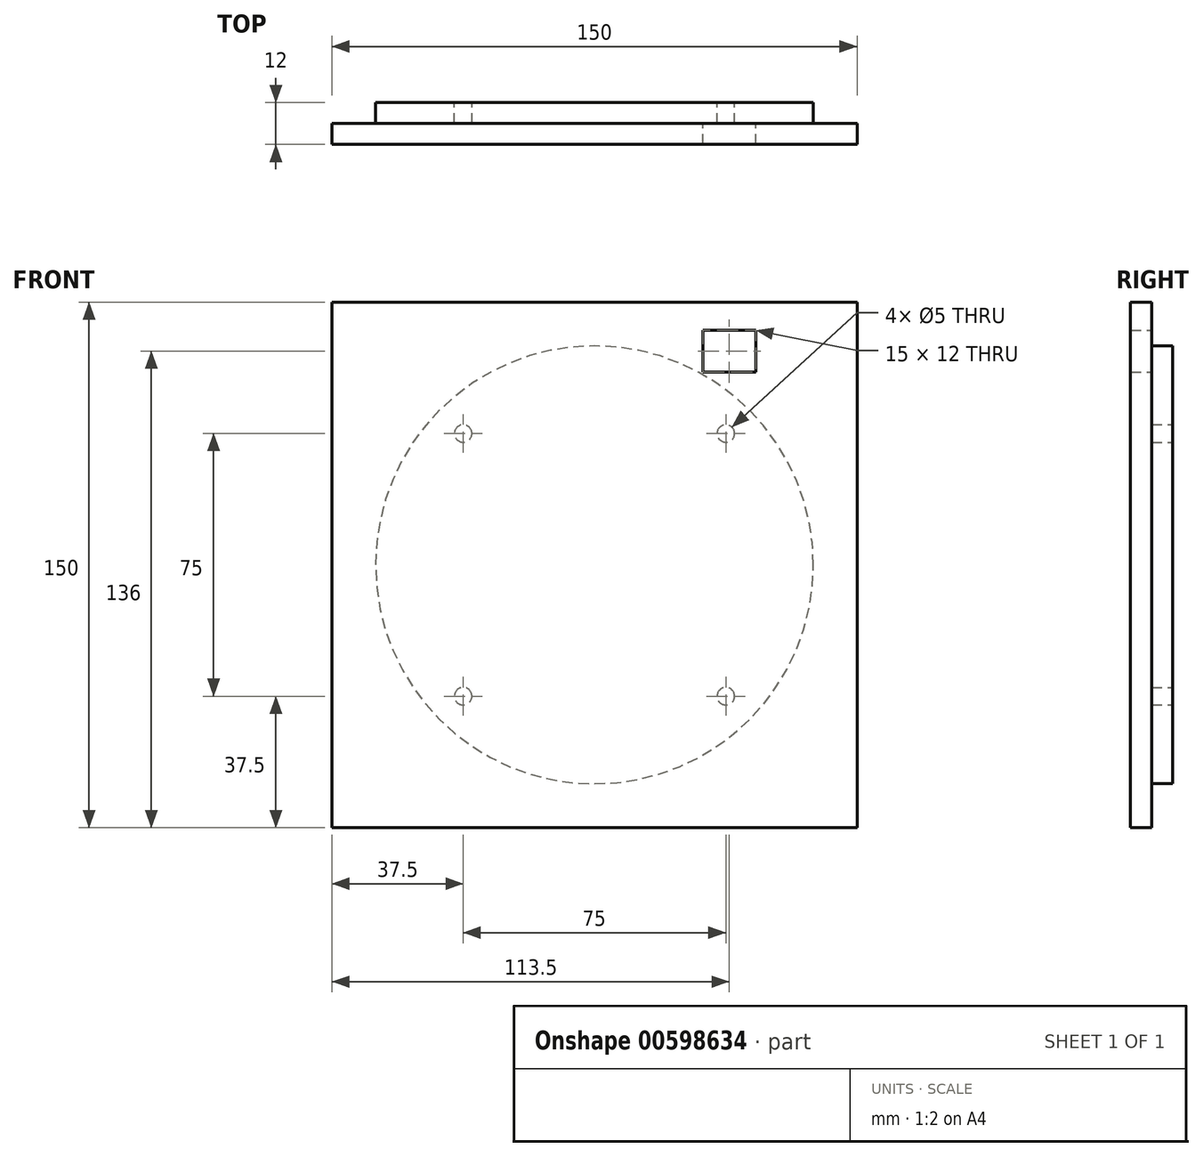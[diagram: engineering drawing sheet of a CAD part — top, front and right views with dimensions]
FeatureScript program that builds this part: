
annotation { "Feature Type Name" : "Feature", "Feature Type Description" : "" }
export const myFeature = defineFeature(function(context is Context, id is Id, definition is map)
    precondition{}
    {
        {
            var Q0;
            Q0=qCreatedBy(makeId("Front.planeOp"),FACE);
            var sketch = newSketch(context, id + "F0", { "sketchPlane" : qUnion([Q0])});
            skLineSegment(sketch, "E0.bottom", {"start": v(60, 60) * mm, "end": v(-60, 60) * mm, "construction": true});
            skLineSegment(sketch, "E0.top", {"start": v(60, -60) * mm, "end": v(-60, -60) * mm, "construction": true});
            skLineSegment(sketch, "E0.left", {"start": v(60, 60) * mm, "end": v(60, -60) * mm, "construction": true});
            skLineSegment(sketch, "E0.right", {"start": v(-60, 60) * mm, "end": v(-60, -60) * mm, "construction": true});
            skPoint(sketch, "E0.middle", {"position": v(0, 0) * mm});
            skCircle(sketch, "E1", {"center": v(0, 0) * mm, "radius": 62.5 * mm});
            skCircle(sketch, "E2", {"center": v(37.5, 37.5) * mm, "radius": 2.5 * mm});
            skCircle(sketch, "E3.0.1.0", {"center": v(37.5, -37.5) * mm, "radius": 2.5 * mm});
            skCircle(sketch, "E3.1.0.0", {"center": v(-37.5, 37.5) * mm, "radius": 2.5 * mm});
            skCircle(sketch, "E3.1.1.0", {"center": v(-37.5, -37.5) * mm, "radius": 2.5 * mm});
            skLineSegment(sketch, "E3.direction1", {"start": v(37.5, 37.5) * mm, "end": v(-37.5, 37.5) * mm, "construction": true});
            skLineSegment(sketch, "E3.direction2", {"start": v(37.5, 37.5) * mm, "end": v(37.5, -37.5) * mm, "construction": true});
            skSolve(sketch);
        }
        {
            var Q0;
            Q0 = qSketchRegion(id + "F0", true);
            extrude(context, id + "F1", {"entities" : qUnion([Q0]), "depth" : 6 * mm, "offsetDistance" : 25 * mm});
        }
        {
            var Q0;
            Q0=makeQuery(id+"F1.opExtrude","CAP_FACE",FACE,{"disambiguationData":[OSD([sQuery(id+"F0.wireOp",EDGE,"E1"),sQuery(id+"F0.wireOp",EDGE,"E2"),sQuery(id+"F0.wireOp",EDGE,"E3.0.1.0"),sQuery(id+"F0.wireOp",EDGE,"E3.1.0.0"),sQuery(id+"F0.wireOp",EDGE,"E3.1.1.0")])],"isStart":false});
            var sketch = newSketch(context, id + "F2", { "sketchPlane" : qUnion([Q0])});
            skLineSegment(sketch, "E4.bottom", {"start": v(75, 75) * mm, "end": v(-75, 75) * mm});
            skLineSegment(sketch, "E4.top", {"start": v(75, -75) * mm, "end": v(-75, -75) * mm});
            skLineSegment(sketch, "E4.left", {"start": v(75, 75) * mm, "end": v(75, -75) * mm});
            skLineSegment(sketch, "E4.right", {"start": v(-75, 75) * mm, "end": v(-75, -75) * mm});
            skPoint(sketch, "E4.middle", {"position": v(0, 0) * mm});
            skLineSegment(sketch, "E5.bottom", {"start": v(60, 60) * mm, "end": v(-60, 60) * mm, "construction": true});
            skLineSegment(sketch, "E5.top", {"start": v(60, -60) * mm, "end": v(-60, -60) * mm, "construction": true});
            skLineSegment(sketch, "E5.left", {"start": v(60, 60) * mm, "end": v(60, -60) * mm, "construction": true});
            skLineSegment(sketch, "E5.right", {"start": v(-60, 60) * mm, "end": v(-60, -60) * mm, "construction": true});
            skLineSegment(sketch, "E6.bottom", {"start": v(31, 67) * mm, "end": v(46, 67) * mm});
            skLineSegment(sketch, "E6.top", {"start": v(31, 55) * mm, "end": v(46, 55) * mm});
            skLineSegment(sketch, "E6.left", {"start": v(31, 67) * mm, "end": v(31, 55) * mm});
            skLineSegment(sketch, "E6.right", {"start": v(46, 67) * mm, "end": v(46, 55) * mm});
            skSolve(sketch);
        }
        {
            var Q0;
            Q0 = qSketchRegion(id + "F2", true);
            extrude(context, id + "F3", {"entities" : qUnion([Q0]), "depth" : 6 * mm, "offsetDistance" : 25 * mm});
        }
    });
